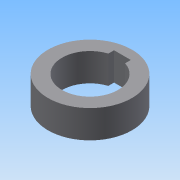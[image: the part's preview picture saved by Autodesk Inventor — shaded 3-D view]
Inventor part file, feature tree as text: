
AUTODESK INVENTOR PART (.ipt)
format: ipt  version: 2015 (Build 190159000, 159)  size: 90,624 bytes
history: native  units: mm
features: extrude x2, sketch x2
ambient origin geometry x8: Origin, YZ Plane, XZ Plane, XY Plane, X Axis, Y Axis, Z Axis, Center Point
bodies: 实体1 (feature_tree)
feature tree (4):
  extrude  "拉伸1"  Depth=20.0mm
  extrude  "拉伸2"  Depth=6.0mm
  sketch  "草图1"  dims[d0=30.0mm d1=20.0mm]
  sketch  "草图2"  dims[d2=10.0mm d3=0.0mm d4=6.0mm d5=1.6mm d6=10.0mm d7=0.0mm]
